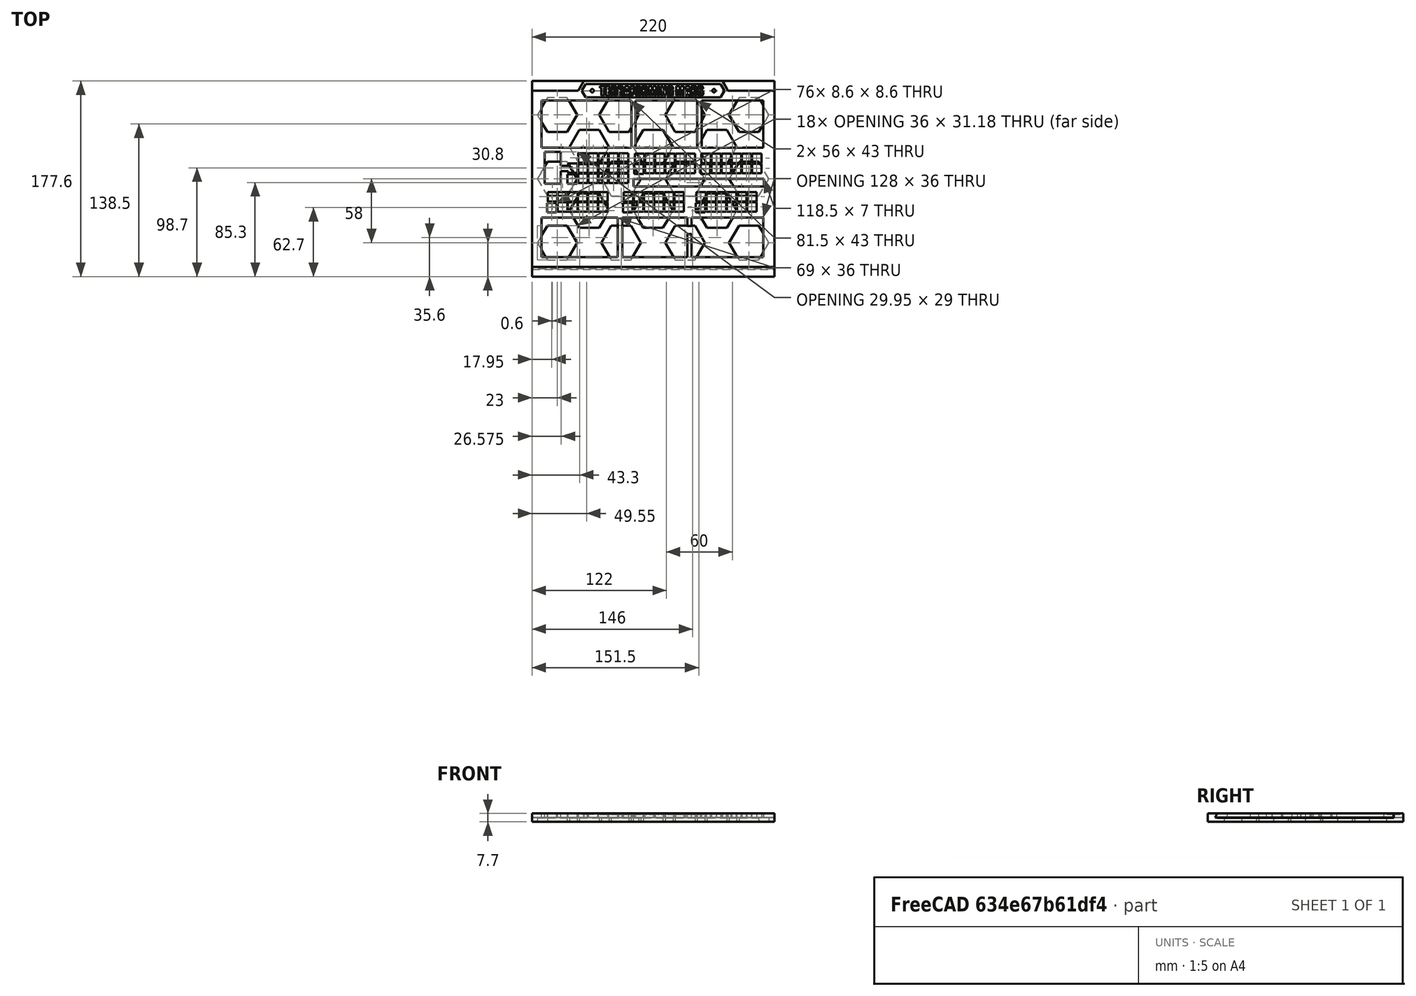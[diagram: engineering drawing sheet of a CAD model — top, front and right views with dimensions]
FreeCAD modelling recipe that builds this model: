
FCSTD DOCUMENT  (FreeCAD 0.21R33668 +26 (Git))
Label: overlay-full-v4
License: All rights reserved
LicenseURL: https://en.wikipedia.org/wiki/All_rights_reserved
objects: Sketcher::SketchObject×11, PartDesign::Pad×9, PartDesign::Pocket×5, Part::Feature×2, Part::Part2DObjectPython×2, PartDesign::Body×2, Mesh::Feature×1, Part::Refine×1, PartDesign::FeatureBase×1, Part::Extrusion×1
note: 48 computed .brp shape members not serialized (recipe doc carries the construction recipe); baked Part::Feature solids carry a one-line shape summary decoded from their .brp

FEATURE [Mesh::Feature] Terraforming_Mars_overlay
FEATURE [Part::Feature] Terraforming_Mars_overlay001
  shape: bbox 208 x 148 x 3.7 mm, 1736 faces, 0 solids (baked)
FEATURE [Part::Feature] Terraforming_Mars_overlay001_solid  label="Terraforming_Mars_overlay001 (Solid)"
  shape: bbox 208 x 148 x 3.7 mm, 1736 faces (baked)
FEATURE [Part::Refine] Terraforming_Mars_overlay001_solid001  label="Terraforming_Mars_overlay001 (Solid)001"
  Source = -> Terraforming_Mars_overlay001_solid
FEATURE [PartDesign::FeatureBase] BaseFeature
  BaseFeature = -> Terraforming_Mars_overlay001_solid001
FEATURE [Sketcher::SketchObject] Sketch
  ExternalGeometry = -> [BaseFeature]
  FullyConstrained = true
  MapMode = 5
  Placement = pos=(0,0,3.7) rot=(0,0,1;0rad)
  Support = -> [BaseFeature]
  sketch-geometry (8):
    g0: LineSegment StartX=6 StartY=154 StartZ=0 EndX=214 EndY=154 EndZ=0
    g1: LineSegment StartX=214 StartY=154 StartZ=0 EndX=214 EndY=6 EndZ=0
    g2: LineSegment StartX=214 StartY=6 StartZ=0 EndX=6 EndY=6 EndZ=0
    g3: LineSegment StartX=6 StartY=6 StartZ=0 EndX=6 EndY=154 EndZ=0
    g4: LineSegment StartX=0 StartY=160 StartZ=0 EndX=220 EndY=160 EndZ=0
    g5: LineSegment StartX=220 StartY=160 StartZ=0 EndX=220 EndY=0 EndZ=0
    g6: LineSegment StartX=220 StartY=0 StartZ=0 EndX=0 EndY=0 EndZ=0
    g7: LineSegment StartX=0 StartY=0 StartZ=0 EndX=0 EndY=160 EndZ=0
  constraints (22):
    c: Coincident(g0,g1)
    c: Coincident(g1,g2)
    c: Coincident(g2,g3)
    c: Coincident(g3,g0)
    c: Horizontal(g0)
    c: Horizontal(g2)
    c: Vertical(g1)
    c: Vertical(g3)
    c: Coincident(g0,g-3)
    c: Coincident(g1,g-4)
    c: Coincident(g4,g5)
    c: Coincident(g5,g6)
    c: Coincident(g6,g7)
    c: Coincident(g7,g4)
    c: Horizontal(g4)
    c: Horizontal(g6)
    c: Vertical(g5)
    c: Vertical(g7)
    c: DistanceX(g4,g0) = 6
    c: DistanceX(g0,g4) = 6
    c: DistanceY(g0,g4) = 6
    c: DistanceY(g5,g1) = 6
FEATURE [PartDesign::Pad] Pad
  BaseFeature = -> BaseFeature
  Direction = (0,0,1)
  Length = 10
  Length2 = 10
  Profile = -> Sketch
  ReferenceAxis = -> Sketch [N_Axis]
  Type = 3
  UpToFace = -> BaseFeature [Face1]
FEATURE [Sketcher::SketchObject] Sketch001
  ExternalGeometry = -> [Pad]
  FullyConstrained = true
  MapMode = 5
  Placement = pos=(0,0,3.7) rot=(0,0,1;0rad)
  Support = -> [Pad]
  sketch-geometry (5):
    g0: GeomPoint X=110 Y=160 Z=0
    g1: LineSegment StartX=42 StartY=160 StartZ=0 EndX=47.0807 EndY=168.8 EndZ=0
    g2: LineSegment StartX=47.0807 StartY=168.8 StartZ=0 EndX=172.919 EndY=168.8 EndZ=0
    g3: LineSegment StartX=172.919 StartY=168.8 StartZ=0 EndX=178 EndY=160 EndZ=0
    g4: LineSegment StartX=178 StartY=160 StartZ=0 EndX=42 EndY=160 EndZ=0
  constraints (13):
    c: Symmetric(g-3,g-3,g0)
    c: Coincident(g1,g2)
    c: Horizontal(g2)
    c: Coincident(g2,g3)
    c: Coincident(g3,g4)
    c: Coincident(g4,g1)
    c: Angle(g1,g4,g1) = 2.0944
    c: Angle(g4,g3,g3) = 2.0944
    c: DistanceY(g1,g1) = 8.8
    c: PointOnObject(g1,g-3)
    c: DistanceX(g-3,g1) = 42
    c: DistanceX(g3,g-3) = 42
    c: PointOnObject(g3,g-3)
FEATURE [PartDesign::Pad] Pad001
  BaseFeature = -> Pad
  Direction = (0,0,1)
  Length = 10
  Length2 = 10
  Profile = -> Sketch001
  ReferenceAxis = -> Sketch001 [N_Axis]
  Type = 3
  UpToFace = -> Pad [Face2]
FEATURE [Sketcher::SketchObject] Sketch002
  ExternalGeometry = -> [Pad001]
  FullyConstrained = true
  MapMode = 5
  Placement = pos=(0,0,3.7) rot=(0,0,1;0rad)
  Support = -> [Pad001]
  sketch-geometry (7):
    g0: GeomPoint X=110 Y=160 Z=0
    g1: LineSegment StartX=45.2332 StartY=160 StartZ=0 EndX=48.6973 EndY=166 EndZ=0
    g2: LineSegment StartX=48.6973 StartY=166 StartZ=0 EndX=171.303 EndY=166 EndZ=0
    g3: LineSegment StartX=171.303 StartY=166 StartZ=0 EndX=174.767 EndY=160 EndZ=0
    g4: LineSegment StartX=174.767 StartY=160 StartZ=0 EndX=171.303 EndY=154 EndZ=0
    g5: LineSegment StartX=171.303 StartY=154 StartZ=0 EndX=48.6973 EndY=154 EndZ=0
    g6: LineSegment StartX=48.6973 StartY=154 StartZ=0 EndX=45.2332 EndY=160 EndZ=0
  constraints (17):
    c: Symmetric(g-4,g-4,g0)
    c: PointOnObject(g1,g-4)
    c: Coincident(g1,g2)
    c: Horizontal(g2)
    c: Coincident(g2,g3)
    c: PointOnObject(g3,g-4)
    c: Coincident(g3,g4)
    c: PointOnObject(g4,g-5)
    c: Coincident(g4,g5)
    c: Coincident(g5,g6)
    c: Coincident(g6,g1)
    c: Parallel(g1,g-6)
    c: Symmetric(g5,g1,g-4)
    c: Symmetric(g4,g2,g-4)
    c: Parallel(g3,g-7)
    c: Distance(g1,g-6) = 2.8
    c: Distance(g2,g-7) = 2.8
FEATURE [PartDesign::Pocket] Pocket
  BaseFeature = -> Pad001
  Direction = (0,0,-1)
  Length = 1
  Length2 = 5
  Profile = -> Sketch002
  ReferenceAxis = -> Sketch002 [N_Axis]
  Type = 0
FEATURE [Part::Part2DObjectPython] ShapeString  # Draft 2D object (typed FeaturePython)
  FontFile = <path>
  MakeFace = true
  Placement = pos=(61.7,155.5,2.7) rot=(0,0,1;0rad)
  Size = 9
  String = TERRAFORMING MARS
  Tracking = 0
FEATURE [Sketcher::SketchObject] Sketch003
  ExternalGeometry = -> [Pocket]
  FullyConstrained = true
  MapMode = 5
  Placement = pos=(0,0,2.7) rot=(0,0,1;0rad)
  Support = -> [Pocket]
  sketch-geometry (3):
    g0: LineSegment StartX=45.2332 StartY=160 StartZ=0 EndX=174.767 EndY=160 EndZ=0
    g1: Circle CenterX=54.7332 CenterY=160 CenterZ=0 NormalX=0 NormalY=0 NormalZ=1 AngleXU=0 Radius=1.5
    g2: Circle CenterX=165.267 CenterY=160 CenterZ=0 NormalX=0 NormalY=0 NormalZ=1 AngleXU=0 Radius=1.5
  constraints (8):
    c: Coincident(g0,g-3)
    c: Coincident(g0,g-4)
    c: PointOnObject(g1,g0)
    c: PointOnObject(g2,g0)
    c: Diameter(g2) = 3
    c: Diameter(g1) = 3
    c: DistanceX(g0,g1) = 9.5
    c: DistanceX(g2,g0) = 9.5
FEATURE [PartDesign::Pad] Pad002
  BaseFeature = -> Pocket
  Direction = (0,0,1)
  Length = 1
  Length2 = 10
  Profile = -> Sketch003
  ReferenceAxis = -> Sketch003 [N_Axis]
  Type = 0
FEATURE [PartDesign::Pad] Pad003
  BaseFeature = -> Pad002
  Direction = (0,-1,0)
  Length = 2
  Length2 = 10
  Profile = -> Pad002 [Face352]
  Type = 0
FEATURE [Sketcher::SketchObject] Sketch004
  ExternalGeometry = -> [Pad003]
  FullyConstrained = true
  MapMode = 5
  Placement = pos=(220,0,0) rot=(0.57735,0.57735,0.57735;2.0944rad)
  Support = -> [Pad003]
  sketch-geometry (3):
    g0: LineSegment StartX=0 StartY=3.7 StartZ=0 EndX=-2 EndY=0 EndZ=0
    g1: LineSegment StartX=-2 StartY=0 StartZ=0 EndX=-2 EndY=3.7 EndZ=0
    g2: LineSegment StartX=-2 StartY=3.7 StartZ=0 EndX=0 EndY=3.7 EndZ=0
  constraints (6):
    c: Coincident(g-4,g0)
    c: Coincident(g0,g-3)
    c: Coincident(g0,g1)
    c: Coincident(g1,g-4)
    c: Coincident(g1,g2)
    c: Coincident(g2,g0)
FEATURE [PartDesign::Pocket] Pocket001
  BaseFeature = -> Pad003
  Direction = (-1,0,0)
  Length = 5
  Length2 = 5
  Profile = -> Sketch004
  ReferenceAxis = -> Sketch004 [N_Axis]
  Type = 1
FEATURE [PartDesign::Body] Body  label="Front"
  BaseFeature = -> Terraforming_Mars_overlay001_solid001
  Group = -> [BaseFeature,Sketch,Pad,Sketch001,Pad001,Sketch002,Pocket,Sketch003,Pad002,Pad003,Sketch004,Pocket001]
  Origin = -> Origin
  Tip = -> Pocket001
FEATURE [Part::Extrusion] Extrude  label="Text"
  Base = -> ShapeString
  Dir = (0,0,1)
  DirMode = 2
  FaceMakerClass = Part::FaceMakerBullseye
  LengthFwd = 1
  LengthRev = 0
  Solid = false
  Symmetric = false
FEATURE [Sketcher::SketchObject] Sketch005
  FullyConstrained = true
  MapMode = 5
  Support = -> [XY_Plane001]
  sketch-geometry (4):
    g0: LineSegment StartX=0 StartY=160 StartZ=0 EndX=220 EndY=160 EndZ=0
    g1: LineSegment StartX=220 StartY=160 StartZ=0 EndX=220 EndY=0 EndZ=0
    g2: LineSegment StartX=220 StartY=0 StartZ=0 EndX=0 EndY=0 EndZ=0
    g3: LineSegment StartX=0 StartY=0 StartZ=0 EndX=0 EndY=160 EndZ=0
  constraints (12):
    c: Coincident(g0,g1)
    c: Coincident(g1,g2)
    c: Coincident(g2,g3)
    c: Coincident(g3,g0)
    c: Horizontal(g0)
    c: Horizontal(g2)
    c: Vertical(g1)
    c: Vertical(g3)
    c: PointOnObject(g1,g-1)
    c: PointOnObject(g0,g-2)
    c: DistanceX(g0,g0) = 220
    c: DistanceY(g1,g1) = 160
FEATURE [PartDesign::Pad] Pad004
  Direction = (0,0,1)
  Length = 4
  Length2 = 10
  Profile = -> Sketch005
  ReferenceAxis = -> Sketch005 [N_Axis]
  Reversed = true
  Type = 0
FEATURE [PartDesign::Pad] Pad005
  BaseFeature = -> Pad004
  Direction = (0,-1,0)
  Length = 8.8
  Length2 = 10
  Profile = -> Pad004 [Face3]
  Type = 0
FEATURE [PartDesign::Pad] Pad006
  BaseFeature = -> Pad005
  Direction = (0,0,1)
  Length = 3.7
  Length2 = 10
  Profile = -> Pad005 [Face8]
  Type = 0
FEATURE [Sketcher::SketchObject] Sketch006
  ExternalGeometry = -> [Pad006]
  FullyConstrained = true
  MapMode = 5
  Placement = pos=(0,0,0) rot=(0.57735,-0.57735,-0.57735;2.0944rad)
  Support = -> [Pad006]
  sketch-geometry (4):
    g0: LineSegment StartX=0 StartY=0 StartZ=0 EndX=2.1 EndY=0 EndZ=0
    g1: LineSegment StartX=0.1 StartY=3.7 StartZ=0 EndX=2.1 EndY=0 EndZ=0
    g2: LineSegment StartX=0 StartY=3.7 StartZ=0 EndX=0 EndY=0 EndZ=0
    g3: LineSegment StartX=0.1 StartY=3.7 StartZ=0 EndX=0 EndY=3.7 EndZ=0
  constraints (10):
    c: Coincident(g-1,g0)
    c: PointOnObject(g0,g-1)
    c: Coincident(g1,g0)
    c: DistanceX(g0,g0) = 2.1
    c: PointOnObject(g1,g-3)
    c: Coincident(g2,g-3)
    c: Coincident(g2,g0)
    c: Coincident(g3,g1)
    c: Coincident(g3,g2)
    c: DistanceX(g3,g3) = 0.1
FEATURE [PartDesign::Pocket] Pocket002
  BaseFeature = -> Pad006
  Direction = (1,0,0)
  Length = 5
  Length2 = 5
  Profile = -> Sketch006
  ReferenceAxis = -> Sketch006 [N_Axis]
  Type = 1
FEATURE [PartDesign::Pad] Pad007
  BaseFeature = -> Pocket002
  Direction = (0,1,0)
  Length = 8.8
  Length2 = 10
  Profile = -> Pocket002 [Face1]
  Type = 0
FEATURE [Sketcher::SketchObject] Sketch007
  ExternalGeometry = -> [Pad007]
  FullyConstrained = true
  MapMode = 5
  Placement = pos=(0,0,0) rot=(0.57735,-0.57735,-0.57735;2.0944rad)
  Support = -> [Pad007]
  sketch-geometry (3):
    g0: LineSegment StartX=4.63784 StartY=3.7 StartZ=0 EndX=8.8 EndY=-4 EndZ=0
    g1: LineSegment StartX=8.8 StartY=-4 StartZ=0 EndX=8.8 EndY=3.7 EndZ=0
    g2: LineSegment StartX=8.8 StartY=3.7 StartZ=0 EndX=4.63784 EndY=3.7 EndZ=0
  constraints (7):
    c: PointOnObject(g0,g-3)
    c: Coincident(g0,g-6)
    c: Coincident(g1,g0)
    c: Coincident(g1,g-5)
    c: Coincident(g2,g1)
    c: Coincident(g2,g0)
    c: Parallel(g0,g-4)
FEATURE [Sketcher::SketchObject] Sketch008
  ExternalGeometry = -> [Pad007]
  FullyConstrained = true
  MapMode = 5
  Support = -> [Pad007]
  sketch-geometry (12):
    g0: LineSegment StartX=0 StartY=160 StartZ=0 EndX=42 EndY=160 EndZ=0
    g1: LineSegment StartX=42 StartY=160 StartZ=0 EndX=47.0807 EndY=168.8 EndZ=0
    g2: LineSegment StartX=0 StartY=168.8 StartZ=0 EndX=46.9652 EndY=168.8 EndZ=0
    g3: LineSegment StartX=46.9652 StartY=168.8 StartZ=0 EndX=41.9423 EndY=160.1 EndZ=0
    g4: LineSegment StartX=41.9423 StartY=160.1 StartZ=0 EndX=0 EndY=160.1 EndZ=0
    g5: LineSegment StartX=0 StartY=160.1 StartZ=0 EndX=0 EndY=168.8 EndZ=0
    g6: LineSegment StartX=172.919 StartY=168.8 StartZ=0 EndX=178 EndY=160 EndZ=0
    g7: LineSegment StartX=178 StartY=160 StartZ=0 EndX=220 EndY=160 EndZ=0
    g8: LineSegment StartX=173.035 StartY=168.8 StartZ=0 EndX=220 EndY=168.8 EndZ=0
    g9: LineSegment StartX=220 StartY=168.8 StartZ=0 EndX=220 EndY=160.1 EndZ=0
    g10: LineSegment StartX=220 StartY=160.1 StartZ=0 EndX=178.058 EndY=160.1 EndZ=0
    g11: LineSegment StartX=178.058 StartY=160.1 StartZ=0 EndX=173.035 EndY=168.8 EndZ=0
  constraints (34):
    c: Coincident(g-4,g0)
    c: PointOnObject(g0,g-4)
    c: Coincident(g0,g1)
    c: PointOnObject(g1,g-3)
    c: DistanceX(g0,g0) = 42
    c: Angle(g-4,g1,g0) = 1.0472
    c: Coincident(g-3,g2)
    c: PointOnObject(g2,g-3)
    c: Coincident(g2,g3)
    c: Coincident(g3,g4)
    c: PointOnObject(g4,g-2)
    c: Horizontal(g4)
    c: Coincident(g4,g5)
    c: Coincident(g5,g2)
    c: Parallel(g3,g1)
    c: Distance(g4,g0) = 0.1
    c: Distance(g2,g1) = 0.1
    c: PointOnObject(g6,g-3)
    c: PointOnObject(g6,g-4)
    c: Coincident(g7,g6)
    c: Coincident(g7,g-5)
    c: DistanceX(g7,g7) = 42
    c: Angle(g6,g-4,g6) = 1.0472
    c: PointOnObject(g8,g-3)
    c: Coincident(g8,g-5)
    c: Coincident(g8,g9)
    c: PointOnObject(g9,g-5)
    c: Coincident(g9,g10)
    c: Horizontal(g10)
    c: Coincident(g10,g11)
    c: Coincident(g11,g8)
    c: Distance(g8,g6) = 0.1
    c: Parallel(g11,g6)
    c: Distance(g9,g7) = 0.1
FEATURE [PartDesign::Pad] Pad008
  BaseFeature = -> Pad007
  Direction = (0,0,1)
  Length = 3.7
  Length2 = 10
  Profile = -> Sketch008
  ReferenceAxis = -> Sketch008 [N_Axis]
  Type = 0
FEATURE [Sketcher::SketchObject] Sketch009
  ExternalGeometry = -> [Pad008]
  FullyConstrained = true
  MapMode = 5
  Support = -> [Pad008]
  sketch-geometry (4):
    g0: LineSegment StartX=0 StartY=0 StartZ=0 EndX=220 EndY=0 EndZ=0
    g1: LineSegment StartX=220 StartY=0 StartZ=0 EndX=220 EndY=160 EndZ=0
    g2: LineSegment StartX=220 StartY=160 StartZ=0 EndX=0 EndY=160 EndZ=0
    g3: LineSegment StartX=0 StartY=160 StartZ=0 EndX=0 EndY=0 EndZ=0
  constraints (10):
    c: Coincident(g0,g1)
    c: Coincident(g1,g2)
    c: Coincident(g2,g3)
    c: Coincident(g3,g0)
    c: Horizontal(g0)
    c: Horizontal(g2)
    c: Vertical(g1)
    c: Vertical(g3)
    c: Coincident(g0,g-5)
    c: Coincident(g1,g-4)
FEATURE [PartDesign::Pocket] Pocket003
  BaseFeature = -> Pad008
  Direction = (0,0,-1)
  Length = 0.3
  Length2 = 5
  Profile = -> Sketch009
  ReferenceAxis = -> Sketch009 [N_Axis]
  Type = 0
FEATURE [Part::Part2DObjectPython] ShapeString001  # Draft 2D object (typed FeaturePython)
  FontFile = <path>
  MakeFace = true
  Placement = pos=(12.35,20,0) rot=(0,0,1;1e-06rad)
  Size = 120
  String = T M
  Tracking = 0
FEATURE [Sketcher::SketchObject] Sketch010
  ExternalGeometry = -> [Pocket003]
  FullyConstrained = true
  MapMode = 5
  Placement = pos=(0,0,-0.3) rot=(0,0,1;0rad)
  Support = -> [Pocket003]
  sketch-geometry (138):
    g0: LineSegment StartX=220 StartY=138 StartZ=0 EndX=0 EndY=138 EndZ=0
    g1: LineSegment StartX=220 StartY=109 StartZ=0 EndX=0 EndY=109 EndZ=0
    g2: LineSegment StartX=220 StartY=80 StartZ=0 EndX=0 EndY=80 EndZ=0
    g3: LineSegment StartX=0 StartY=51 StartZ=0 EndX=220 EndY=51 EndZ=0
    g4: LineSegment StartX=70 StartY=109 StartZ=0 EndX=61 EndY=124.588 EndZ=0
    g5: LineSegment StartX=61 StartY=124.588 StartZ=0 EndX=43 EndY=124.588 EndZ=0
    g6: LineSegment StartX=43 StartY=124.588 StartZ=0 EndX=34 EndY=109 EndZ=0
    g7: LineSegment StartX=34 StartY=109 StartZ=0 EndX=43 EndY=93.4115 EndZ=0
    g8: LineSegment StartX=43 StartY=93.4115 StartZ=0 EndX=61 EndY=93.4115 EndZ=0
    g9: LineSegment StartX=61 StartY=93.4115 StartZ=0 EndX=70 EndY=109 EndZ=0
    g10: Circle CenterX=52 CenterY=109 CenterZ=0 NormalX=0 NormalY=0 NormalZ=1 AngleXU=0 Radius=18
    g11: LineSegment StartX=41 StartY=138 StartZ=0 EndX=32 EndY=153.588 EndZ=0
    g12: LineSegment StartX=32 StartY=153.588 StartZ=0 EndX=14 EndY=153.588 EndZ=0
    g13: LineSegment StartX=14 StartY=153.588 StartZ=0 EndX=5 EndY=138 EndZ=0
    g14: LineSegment StartX=5 StartY=138 StartZ=0 EndX=14 EndY=122.412 EndZ=0
    g15: LineSegment StartX=14 StartY=122.412 StartZ=0 EndX=32 EndY=122.412 EndZ=0
    g16: LineSegment StartX=32 StartY=122.412 StartZ=0 EndX=41 EndY=138 EndZ=0
    g17: Circle CenterX=23 CenterY=138 CenterZ=0 NormalX=0 NormalY=0 NormalZ=1 AngleXU=0 Radius=18
    g18: LineSegment StartX=97 StartY=138 StartZ=0 EndX=88 EndY=153.588 EndZ=0
    g19: LineSegment StartX=88 StartY=153.588 StartZ=0 EndX=70 EndY=153.588 EndZ=0
    g20: LineSegment StartX=70 StartY=153.588 StartZ=0 EndX=61 EndY=138 EndZ=0
    g21: LineSegment StartX=61 StartY=138 StartZ=0 EndX=70 EndY=122.412 EndZ=0
    g22: LineSegment StartX=70 StartY=122.412 StartZ=0 EndX=88 EndY=122.412 EndZ=0
    g23: LineSegment StartX=88 StartY=122.412 StartZ=0 EndX=97 EndY=138 EndZ=0
    g24: Circle CenterX=79 CenterY=138 CenterZ=0 NormalX=0 NormalY=0 NormalZ=1 AngleXU=0 Radius=18
    g25: LineSegment StartX=0 StartY=22 StartZ=0 EndX=220 EndY=22 EndZ=0
    g26: LineSegment StartX=128 StartY=109 StartZ=0 EndX=119 EndY=124.588 EndZ=0
    g27: LineSegment StartX=119 StartY=124.588 StartZ=0 EndX=101 EndY=124.588 EndZ=0
    g28: LineSegment StartX=101 StartY=124.588 StartZ=0 EndX=92 EndY=109 EndZ=0
    g29: LineSegment StartX=92 StartY=109 StartZ=0 EndX=101 EndY=93.4115 EndZ=0
    g30: LineSegment StartX=101 StartY=93.4115 StartZ=0 EndX=119 EndY=93.4115 EndZ=0
    g31: LineSegment StartX=119 StartY=93.4115 StartZ=0 EndX=128 EndY=109 EndZ=0
    g32: Circle CenterX=110 CenterY=109 CenterZ=0 NormalX=0 NormalY=0 NormalZ=1 AngleXU=0 Radius=18
    g33: LineSegment StartX=157 StartY=138 StartZ=0 EndX=148 EndY=153.588 EndZ=0
    g34: LineSegment StartX=148 StartY=153.588 StartZ=0 EndX=130 EndY=153.588 EndZ=0
    g35: LineSegment StartX=130 StartY=153.588 StartZ=0 EndX=121 EndY=138 EndZ=0
    g36: LineSegment StartX=121 StartY=138 StartZ=0 EndX=130 EndY=122.412 EndZ=0
    g37: LineSegment StartX=130 StartY=122.412 StartZ=0 EndX=148 EndY=122.412 EndZ=0
    g38: LineSegment StartX=148 StartY=122.412 StartZ=0 EndX=157 EndY=138 EndZ=0
    g39: Circle CenterX=139 CenterY=138 CenterZ=0 NormalX=0 NormalY=0 NormalZ=1 AngleXU=0 Radius=18
    g40: LineSegment StartX=23 StartY=160 StartZ=0 EndX=23 EndY=0 EndZ=0
    g41: LineSegment StartX=52 StartY=160 StartZ=0 EndX=52 EndY=0 EndZ=0
    g42: LineSegment StartX=81 StartY=160 StartZ=0 EndX=81 EndY=0 EndZ=0
    g43: LineSegment StartX=110 StartY=160 StartZ=0 EndX=110 EndY=0 EndZ=0
    g44: LineSegment StartX=139 StartY=160 StartZ=0 EndX=139 EndY=0 EndZ=0
    g45: LineSegment StartX=168 StartY=160 StartZ=0 EndX=168 EndY=0 EndZ=0
    g46: LineSegment StartX=197 StartY=160 StartZ=0 EndX=197 EndY=0 EndZ=0
    g47: LineSegment StartX=186 StartY=109 StartZ=0 EndX=177 EndY=124.588 EndZ=0
    g48: LineSegment StartX=177 StartY=124.588 StartZ=0 EndX=159 EndY=124.588 EndZ=0
    g49: LineSegment StartX=159 StartY=124.588 StartZ=0 EndX=150 EndY=109 EndZ=0
    g50: LineSegment StartX=150 StartY=109 StartZ=0 EndX=159 EndY=93.4115 EndZ=0
    g51: LineSegment StartX=159 StartY=93.4115 StartZ=0 EndX=177 EndY=93.4115 EndZ=0
    g52: LineSegment StartX=177 StartY=93.4115 StartZ=0 EndX=186 EndY=109 EndZ=0
    g53: Circle CenterX=168 CenterY=109 CenterZ=0 NormalX=0 NormalY=0 NormalZ=1 AngleXU=0 Radius=18
    g54: LineSegment StartX=215 StartY=138 StartZ=0 EndX=206 EndY=153.588 EndZ=0
    g55: LineSegment StartX=206 StartY=153.588 StartZ=0 EndX=188 EndY=153.588 EndZ=0
    g56: LineSegment StartX=188 StartY=153.588 StartZ=0 EndX=179 EndY=138 EndZ=0
    g57: LineSegment StartX=179 StartY=138 StartZ=0 EndX=188 EndY=122.412 EndZ=0
    g58: LineSegment StartX=188 StartY=122.412 StartZ=0 EndX=206 EndY=122.412 EndZ=0
    g59: LineSegment StartX=206 StartY=122.412 StartZ=0 EndX=215 EndY=138 EndZ=0
    g60: Circle CenterX=197 CenterY=138 CenterZ=0 NormalX=0 NormalY=0 NormalZ=1 AngleXU=0 Radius=18
    g61: LineSegment StartX=215 StartY=80 StartZ=0 EndX=206 EndY=95.5885 EndZ=0
    g62: LineSegment StartX=206 StartY=95.5885 StartZ=0 EndX=188 EndY=95.5885 EndZ=0
    g63: LineSegment StartX=188 StartY=95.5885 StartZ=0 EndX=179 EndY=80 EndZ=0
    g64: LineSegment StartX=179 StartY=80 StartZ=0 EndX=188 EndY=64.4115 EndZ=0
    g65: LineSegment StartX=188 StartY=64.4115 StartZ=0 EndX=206 EndY=64.4115 EndZ=0
    g66: LineSegment StartX=206 StartY=64.4115 StartZ=0 EndX=215 EndY=80 EndZ=0
    g67: Circle CenterX=197 CenterY=80 CenterZ=0 NormalX=0 NormalY=0 NormalZ=1 AngleXU=0 Radius=18
    g68: LineSegment StartX=186 StartY=51 StartZ=0 EndX=177 EndY=66.5885 EndZ=0
    g69: LineSegment StartX=177 StartY=66.5885 StartZ=0 EndX=159 EndY=66.5885 EndZ=0
    g70: LineSegment StartX=159 StartY=66.5885 StartZ=0 EndX=150 EndY=51 EndZ=0
    g71: LineSegment StartX=150 StartY=51 StartZ=0 EndX=159 EndY=35.4115 EndZ=0
    g72: LineSegment StartX=159 StartY=35.4115 StartZ=0 EndX=177 EndY=35.4115 EndZ=0
    g73: LineSegment StartX=177 StartY=35.4115 StartZ=0 EndX=186 EndY=51 EndZ=0
    g74: Circle CenterX=168 CenterY=51 CenterZ=0 NormalX=0 NormalY=0 NormalZ=1 AngleXU=0 Radius=18
    g75: LineSegment StartX=157 StartY=80 StartZ=0 EndX=148 EndY=95.5885 EndZ=0
    g76: LineSegment StartX=148 StartY=95.5885 StartZ=0 EndX=130 EndY=95.5885 EndZ=0
    g77: LineSegment StartX=130 StartY=95.5885 StartZ=0 EndX=121 EndY=80 EndZ=0
    g78: LineSegment StartX=121 StartY=80 StartZ=0 EndX=130 EndY=64.4115 EndZ=0
    g79: LineSegment StartX=130 StartY=64.4115 StartZ=0 EndX=148 EndY=64.4115 EndZ=0
    g80: LineSegment StartX=148 StartY=64.4115 StartZ=0 EndX=157 EndY=80 EndZ=0
    g81: Circle CenterX=139 CenterY=80 CenterZ=0 NormalX=0 NormalY=0 NormalZ=1 AngleXU=0 Radius=18
    g82: LineSegment StartX=99 StartY=80 StartZ=0 EndX=90 EndY=95.5885 EndZ=0
    g83: LineSegment StartX=90 StartY=95.5885 StartZ=0 EndX=72 EndY=95.5885 EndZ=0
    g84: LineSegment StartX=72 StartY=95.5885 StartZ=0 EndX=63 EndY=80 EndZ=0
    g85: LineSegment StartX=63 StartY=80 StartZ=0 EndX=72 EndY=64.4115 EndZ=0
    g86: LineSegment StartX=72 StartY=64.4115 StartZ=0 EndX=90 EndY=64.4115 EndZ=0
    g87: LineSegment StartX=90 StartY=64.4115 StartZ=0 EndX=99 EndY=80 EndZ=0
    g88: Circle CenterX=81 CenterY=80 CenterZ=0 NormalX=0 NormalY=0 NormalZ=1 AngleXU=0 Radius=18
    g89: LineSegment StartX=41 StartY=80 StartZ=0 EndX=32 EndY=95.5885 EndZ=0
    g90: LineSegment StartX=32 StartY=95.5885 StartZ=0 EndX=14 EndY=95.5885 EndZ=0
    g91: LineSegment StartX=14 StartY=95.5885 StartZ=0 EndX=5 EndY=80 EndZ=0
    g92: LineSegment StartX=5 StartY=80 StartZ=0 EndX=14 EndY=64.4115 EndZ=0
    g93: LineSegment StartX=14 StartY=64.4115 StartZ=0 EndX=32 EndY=64.4115 EndZ=0
    g94: LineSegment StartX=32 StartY=64.4115 StartZ=0 EndX=41 EndY=80 EndZ=0
    g95: Circle CenterX=23 CenterY=80 CenterZ=0 NormalX=0 NormalY=0 NormalZ=1 AngleXU=0 Radius=18
    g96: LineSegment StartX=70 StartY=51 StartZ=0 EndX=61 EndY=66.5885 EndZ=0
    g97: LineSegment StartX=61 StartY=66.5885 StartZ=0 EndX=43 EndY=66.5885 EndZ=0
    g98: LineSegment StartX=43 StartY=66.5885 StartZ=0 EndX=34 EndY=51 EndZ=0
    g99: LineSegment StartX=34 StartY=51 StartZ=0 EndX=43 EndY=35.4115 EndZ=0
    g100: LineSegment StartX=43 StartY=35.4115 StartZ=0 EndX=61 EndY=35.4115 EndZ=0
    g101: LineSegment StartX=61 StartY=35.4115 StartZ=0 EndX=70 EndY=51 EndZ=0
    g102: Circle CenterX=52 CenterY=51 CenterZ=0 NormalX=0 NormalY=0 NormalZ=1 AngleXU=0 Radius=18
    g103: LineSegment StartX=128 StartY=51 StartZ=0 EndX=119 EndY=66.5885 EndZ=0
    g104: LineSegment StartX=119 StartY=66.5885 StartZ=0 EndX=101 EndY=66.5885 EndZ=0
    g105: LineSegment StartX=101 StartY=66.5885 StartZ=0 EndX=92 EndY=51 EndZ=0
    g106: LineSegment StartX=92 StartY=51 StartZ=0 EndX=101 EndY=35.4115 EndZ=0
    g107: LineSegment StartX=101 StartY=35.4115 StartZ=0 EndX=119 EndY=35.4115 EndZ=0
    g108: LineSegment StartX=119 StartY=35.4115 StartZ=0 EndX=128 EndY=51 EndZ=0
    g109: Circle CenterX=110 CenterY=51 CenterZ=0 NormalX=0 NormalY=0 NormalZ=1 AngleXU=0 Radius=18
    g110: LineSegment StartX=41 StartY=22 StartZ=0 EndX=32 EndY=37.5885 EndZ=0
    g111: LineSegment StartX=32 StartY=37.5885 StartZ=0 EndX=14 EndY=37.5885 EndZ=0
    g112: LineSegment StartX=14 StartY=37.5885 StartZ=0 EndX=5 EndY=22 EndZ=0
    g113: LineSegment StartX=5 StartY=22 StartZ=0 EndX=14 EndY=6.41154 EndZ=0
    g114: LineSegment StartX=14 StartY=6.41154 StartZ=0 EndX=32 EndY=6.41154 EndZ=0
    g115: LineSegment StartX=32 StartY=6.41154 StartZ=0 EndX=41 EndY=22 EndZ=0
    g116: Circle CenterX=23 CenterY=22 CenterZ=0 NormalX=0 NormalY=0 NormalZ=1 AngleXU=0 Radius=18
    g117: LineSegment StartX=99 StartY=22 StartZ=0 EndX=90 EndY=37.5885 EndZ=0
    g118: LineSegment StartX=90 StartY=37.5885 StartZ=0 EndX=72 EndY=37.5885 EndZ=0
    g119: LineSegment StartX=72 StartY=37.5885 StartZ=0 EndX=63 EndY=22 EndZ=0
    g120: LineSegment StartX=63 StartY=22 StartZ=0 EndX=72 EndY=6.41154 EndZ=0
    g121: LineSegment StartX=72 StartY=6.41154 StartZ=0 EndX=90 EndY=6.41154 EndZ=0
    g122: LineSegment StartX=90 StartY=6.41154 StartZ=0 EndX=99 EndY=22 EndZ=0
    g123: Circle CenterX=81 CenterY=22 CenterZ=0 NormalX=0 NormalY=0 NormalZ=1 AngleXU=0 Radius=18
    g124: LineSegment StartX=157 StartY=22 StartZ=0 EndX=148 EndY=37.5885 EndZ=0
    g125: LineSegment StartX=148 StartY=37.5885 StartZ=0 EndX=130 EndY=37.5885 EndZ=0
    g126: LineSegment StartX=130 StartY=37.5885 StartZ=0 EndX=121 EndY=22 EndZ=0
    g127: LineSegment StartX=121 StartY=22 StartZ=0 EndX=130 EndY=6.41154 EndZ=0
    g128: LineSegment StartX=130 StartY=6.41154 StartZ=0 EndX=148 EndY=6.41154 EndZ=0
    g129: LineSegment StartX=148 StartY=6.41154 StartZ=0 EndX=157 EndY=22 EndZ=0
    g130: Circle CenterX=139 CenterY=22 CenterZ=0 NormalX=0 NormalY=0 NormalZ=1 AngleXU=0 Radius=18
    g131: LineSegment StartX=215 StartY=22 StartZ=0 EndX=206 EndY=37.5885 EndZ=0
    g132: LineSegment StartX=206 StartY=37.5885 StartZ=0 EndX=188 EndY=37.5885 EndZ=0
    g133: LineSegment StartX=188 StartY=37.5885 StartZ=0 EndX=179 EndY=22 EndZ=0
    g134: LineSegment StartX=179 StartY=22 StartZ=0 EndX=188 EndY=6.41154 EndZ=0
    g135: LineSegment StartX=188 StartY=6.41154 StartZ=0 EndX=206 EndY=6.41154 EndZ=0
    g136: LineSegment StartX=206 StartY=6.41154 StartZ=0 EndX=215 EndY=22 EndZ=0
    g137: Circle CenterX=197 CenterY=22 CenterZ=0 NormalX=0 NormalY=0 NormalZ=1 AngleXU=0 Radius=18
  constraints (354):
    c: PointOnObject(g0,g-5)
    c: Horizontal(g0)
    c: PointOnObject(g1,g-5)
    c: PointOnObject(g1,g-3)
    c: Horizontal(g1)
    c: PointOnObject(g2,g-5)
    c: PointOnObject(g2,g-2)
    c: Horizontal(g2)
    c: PointOnObject(g0,g-3)
    c: DistanceY(g0,g-4) = 22
    c: DistanceY(g1,g0) = 29
    c: DistanceY(g2,g1) = 29
    c: PointOnObject(g3,g-3)
    c: PointOnObject(g3,g-5)
    c: Horizontal(g3)
    c: DistanceY(g3,g2) = 29
    c: Coincident(g4,g5)
    c: Coincident(g5,g6)
    c: Coincident(g6,g7)
    c: Coincident(g7,g8)
    c: Coincident(g8,g9)
    c: Coincident(g9,g4)
    c: Equal(g4, g5-g9) x5
    c: PointOnObject(g4,g10)
    c: PointOnObject(g5,g10)
    c: PointOnObject(g6,g10)
    c: PointOnObject(g7,g10)
    c: PointOnObject(g8,g10)
    c: PointOnObject(g9,g10)
    c: PointOnObject(g10,g1)
    c: PointOnObject(g9,g1)
    c: Coincident(g11,g12)
    c: Coincident(g12,g13)
    c: Coincident(g13,g14)
    c: Coincident(g14,g15)
    c: Coincident(g15,g16)
    c: Coincident(g16,g11)
    c: Equal(g11, g12-g16) x5
    c: PointOnObject(g11,g17)
    c: PointOnObject(g12,g17)
    c: PointOnObject(g13,g17)
    c: PointOnObject(g14,g17)
    c: PointOnObject(g15,g17)
    c: PointOnObject(g16,g17)
    c: PointOnObject(g17,g0)
    c: PointOnObject(g16,g0)
    c: Coincident(g18,g19)
    c: Coincident(g19,g20)
    c: Coincident(g20,g21)
    c: Coincident(g21,g22)
    c: Coincident(g22,g23)
    c: Coincident(g23,g18)
    c: Equal(g18, g19-g23) x5
    c: PointOnObject(g18,g24)
    c: PointOnObject(g19,g24)
    c: PointOnObject(g20,g24)
    c: PointOnObject(g21,g24)
    c: PointOnObject(g22,g24)
    c: PointOnObject(g23,g24)
    c: PointOnObject(g24,g0)
    c: PointOnObject(g23,g0)
    c: PointOnObject(g25,g-3)
    c: PointOnObject(g25,g-5)
    c: Horizontal(g25)
    c: DistanceY(g25,g3) = 29
    c: Coincident(g26,g27)
    c: Coincident(g27,g28)
    c: Coincident(g28,g29)
    c: Coincident(g29,g30)
    c: Coincident(g30,g31)
    c: Coincident(g31,g26)
    c: Equal(g26, g27-g31) x5
    c: PointOnObject(g26,g32)
    c: PointOnObject(g27,g32)
    c: PointOnObject(g28,g32)
    c: PointOnObject(g29,g32)
    c: PointOnObject(g30,g32)
    c: PointOnObject(g31,g32)
    c: PointOnObject(g32,g1)
    c: PointOnObject(g31,g1)
    c: Coincident(g33,g34)
    c: Coincident(g34,g35)
    c: Coincident(g35,g36)
    c: Coincident(g36,g37)
    c: Coincident(g37,g38)
    c: Coincident(g38,g33)
    c: Equal(g33, g34-g38) x5
    c: PointOnObject(g33,g39)
    c: PointOnObject(g34,g39)
    c: PointOnObject(g35,g39)
    c: PointOnObject(g36,g39)
    c: PointOnObject(g37,g39)
    c: PointOnObject(g38,g39)
    c: PointOnObject(g39,g0)
    c: PointOnObject(g38,g0)
    c: DistanceX(g24,g39) = 60
    c: PointOnObject(g40,g-4)
    c: PointOnObject(g40,g-6)
    c: Vertical(g40)
    c: PointOnObject(g41,g-4)
    c: PointOnObject(g41,g-6)
    c: Vertical(g41)
    c: PointOnObject(g42,g-4)
    c: PointOnObject(g42,g-6)
    c: Vertical(g42)
    c: PointOnObject(g43,g-4)
    c: PointOnObject(g43,g-6)
    c: Vertical(g43)
    c: PointOnObject(g44,g-4)
    c: PointOnObject(g44,g-6)
    c: Vertical(g44)
    c: PointOnObject(g45,g-4)
    c: PointOnObject(g45,g-6)
    c: Vertical(g45)
    c: PointOnObject(g46,g-4)
    c: PointOnObject(g46,g-6)
    c: Vertical(g46)
    c: DistanceX(g40,g41) = 29
    c: DistanceX(g41,g42) = 29
    c: DistanceX(g42,g43) = 29
    c: DistanceX(g43,g44) = 29
    c: DistanceX(g44,g45) = 29
    c: DistanceX(g45,g46) = 29
    c: DistanceX(g-4,g40) = 23
    c: PointOnObject(g17,g40)
    c: Radius(g17) = 18
    c: PointOnObject(g10,g41)
    c: Radius(g10) = 18
    c: Radius(g24) = 18
    c: Radius(g32) = 18
    c: Radius(g39) = 18
    c: PointOnObject(g32,g43)
    c: PointOnObject(g39,g44)
    c: Coincident(g47,g48)
    c: Coincident(g48,g49)
    c: Coincident(g49,g50)
    c: Coincident(g50,g51)
    c: Coincident(g51,g52)
    c: Coincident(g52,g47)
    c: Equal(g47, g48-g52) x5
    c: PointOnObject(g47,g53)
    c: PointOnObject(g48,g53)
    c: PointOnObject(g49,g53)
    c: PointOnObject(g50,g53)
    c: PointOnObject(g51,g53)
    c: PointOnObject(g52,g53)
    c: PointOnObject(g53,g1)
    c: PointOnObject(g52,g1)
    c: Coincident(g54,g55)
    c: Coincident(g55,g56)
    c: Coincident(g56,g57)
    c: Coincident(g57,g58)
    c: Coincident(g58,g59)
    c: Coincident(g59,g54)
    c: Equal(g54, g55-g59) x5
    c: PointOnObject(g54,g60)
    c: PointOnObject(g55,g60)
    c: PointOnObject(g56,g60)
    c: PointOnObject(g57,g60)
    c: PointOnObject(g58,g60)
    c: PointOnObject(g59,g60)
    c: PointOnObject(g60,g0)
    c: PointOnObject(g59,g0)
    c: Coincident(g61,g62)
    c: Coincident(g62,g63)
    c: Coincident(g63,g64)
    c: Coincident(g64,g65)
    c: Coincident(g65,g66)
    c: Coincident(g66,g61)
    c: Equal(g61, g62-g66) x5
    c: PointOnObject(g61,g67)
    c: PointOnObject(g62,g67)
    c: PointOnObject(g63,g67)
    c: PointOnObject(g64,g67)
    c: PointOnObject(g65,g67)
    c: PointOnObject(g66,g67)
    c: PointOnObject(g67,g2)
    c: PointOnObject(g66,g2)
    c: Coincident(g68,g69)
    c: Coincident(g69,g70)
    c: Coincident(g70,g71)
    c: Coincident(g71,g72)
    c: Coincident(g72,g73)
    c: Coincident(g73,g68)
    c: Equal(g68, g69-g73) x5
    c: PointOnObject(g68,g74)
    c: PointOnObject(g69,g74)
    c: PointOnObject(g70,g74)
    c: PointOnObject(g71,g74)
    c: PointOnObject(g72,g74)
    c: PointOnObject(g73,g74)
    c: PointOnObject(g74,g3)
    c: PointOnObject(g73,g3)
    c: Coincident(g75,g76)
    c: Coincident(g76,g77)
    c: Coincident(g77,g78)
    c: Coincident(g78,g79)
    c: Coincident(g79,g80)
    c: Coincident(g80,g75)
    c: Equal(g75, g76-g80) x5
    c: PointOnObject(g75,g81)
    c: PointOnObject(g76,g81)
    c: PointOnObject(g77,g81)
    c: PointOnObject(g78,g81)
    c: PointOnObject(g79,g81)
    c: PointOnObject(g80,g81)
    c: PointOnObject(g81,g2)
    c: PointOnObject(g80,g2)
    c: Coincident(g82,g83)
    c: Coincident(g83,g84)
    c: Coincident(g84,g85)
    c: Coincident(g85,g86)
    c: Coincident(g86,g87)
    c: Coincident(g87,g82)
    c: Equal(g82, g83-g87) x5
    c: PointOnObject(g82,g88)
    c: PointOnObject(g83,g88)
    c: PointOnObject(g84,g88)
    c: PointOnObject(g85,g88)
    c: PointOnObject(g86,g88)
    c: PointOnObject(g87,g88)
    c: PointOnObject(g88,g2)
    c: PointOnObject(g87,g2)
    c: Coincident(g89,g90)
    c: Coincident(g90,g91)
    c: Coincident(g91,g92)
    c: Coincident(g92,g93)
    c: Coincident(g93,g94)
    c: Coincident(g94,g89)
    c: Equal(g89, g90-g94) x5
    c: PointOnObject(g89,g95)
    c: PointOnObject(g90,g95)
    c: PointOnObject(g91,g95)
    c: PointOnObject(g92,g95)
    c: PointOnObject(g93,g95)
    c: PointOnObject(g94,g95)
    c: PointOnObject(g95,g2)
    c: PointOnObject(g94,g2)
    c: Coincident(g96,g97)
    c: Coincident(g97,g98)
    c: Coincident(g98,g99)
    c: Coincident(g99,g100)
    c: Coincident(g100,g101)
    c: Coincident(g101,g96)
    c: Equal(g96, g97-g101) x5
    c: PointOnObject(g96,g102)
    c: PointOnObject(g97,g102)
    c: PointOnObject(g98,g102)
    c: PointOnObject(g99,g102)
    c: PointOnObject(g100,g102)
    c: PointOnObject(g101,g102)
    c: PointOnObject(g102,g3)
    c: PointOnObject(g101,g3)
    c: Coincident(g103,g104)
    c: Coincident(g104,g105)
    c: Coincident(g105,g106)
    c: Coincident(g106,g107)
    c: Coincident(g107,g108)
    c: Coincident(g108,g103)
    c: Equal(g103, g104-g108) x5
    c: PointOnObject(g103,g109)
    c: PointOnObject(g104,g109)
    c: PointOnObject(g105,g109)
    c: PointOnObject(g106,g109)
    c: PointOnObject(g107,g109)
    c: PointOnObject(g108,g109)
    c: PointOnObject(g109,g3)
    c: PointOnObject(g108,g3)
    c: Coincident(g110,g111)
    c: Coincident(g111,g112)
    c: Coincident(g112,g113)
    c: Coincident(g113,g114)
    c: Coincident(g114,g115)
    c: Coincident(g115,g110)
    c: Equal(g110, g111-g115) x5
    c: PointOnObject(g110,g116)
    c: PointOnObject(g111,g116)
    c: PointOnObject(g112,g116)
    c: PointOnObject(g113,g116)
    c: PointOnObject(g114,g116)
    c: PointOnObject(g115,g116)
    c: PointOnObject(g116,g25)
    c: PointOnObject(g115,g25)
    c: Coincident(g117,g118)
    c: Coincident(g118,g119)
    c: Coincident(g119,g120)
    c: Coincident(g120,g121)
    c: Coincident(g121,g122)
    c: Coincident(g122,g117)
    c: Equal(g117, g118-g122) x5
    c: PointOnObject(g117,g123)
    c: PointOnObject(g118,g123)
    c: PointOnObject(g119,g123)
    c: PointOnObject(g120,g123)
    c: PointOnObject(g121,g123)
    c: PointOnObject(g122,g123)
    c: PointOnObject(g123,g25)
    c: PointOnObject(g122,g25)
    c: Coincident(g124,g125)
    c: Coincident(g125,g126)
    c: Coincident(g126,g127)
    c: Coincident(g127,g128)
    c: Coincident(g128,g129)
    c: Coincident(g129,g124)
    c: Equal(g124, g125-g129) x5
    c: PointOnObject(g124,g130)
    c: PointOnObject(g125,g130)
    c: PointOnObject(g126,g130)
    c: PointOnObject(g127,g130)
    c: PointOnObject(g128,g130)
    c: PointOnObject(g129,g130)
    c: PointOnObject(g130,g25)
    c: PointOnObject(g129,g25)
    c: Coincident(g131,g132)
    c: Coincident(g132,g133)
    c: Coincident(g133,g134)
    c: Coincident(g134,g135)
    c: Coincident(g135,g136)
    c: Coincident(g136,g131)
    c: Equal(g131, g132-g136) x5
    c: PointOnObject(g131,g137)
    c: PointOnObject(g132,g137)
    c: PointOnObject(g133,g137)
    c: PointOnObject(g134,g137)
    c: PointOnObject(g135,g137)
    c: PointOnObject(g136,g137)
    c: PointOnObject(g137,g25)
    c: PointOnObject(g136,g25)
    c: PointOnObject(g67,g46)
    c: PointOnObject(g81,g44)
    c: PointOnObject(g88,g42)
    c: PointOnObject(g95,g40)
    c: PointOnObject(g102,g41)
    c: PointOnObject(g109,g43)
    c: PointOnObject(g74,g45)
    c: PointOnObject(g137,g46)
    c: PointOnObject(g130,g44)
    c: PointOnObject(g123,g42)
    c: PointOnObject(g116,g40)
    c: Radius(g95) = 18
    c: Radius(g88) = 18
    c: Radius(g81) = 18
    c: Radius(g53) = 18
    c: Radius(g60) = 18
    c: Radius(g67) = 18
    c: Radius(g74) = 18
    c: Radius(g109) = 18
    c: Radius(g102) = 18
    c: Radius(g116) = 18
    c: Radius(g123) = 18
    c: Radius(g130) = 18
    c: Radius(g137) = 18
    c: PointOnObject(g53,g45)
    c: PointOnObject(g60,g46)
FEATURE [PartDesign::Pocket] Pocket004
  BaseFeature = -> Pocket003
  Direction = (0,0,-1)
  Length = 5
  Length2 = 5
  Profile = -> Sketch010
  ReferenceAxis = -> Sketch010 [N_Axis]
  Type = 1
FEATURE [PartDesign::Body] Body001  label="Back"
  Group = -> [Sketch005,Pad004,Pad005,Pad006,Sketch006,Pocket002,Pad007,Sketch007,Sketch008,Pad008,Sketch009,Pocket003,Sketch010,Pocket004]
  Origin = -> Origin001
  Tip = -> Pocket004
note: 2 file-system paths scrubbed to <path> (originals preserved in the JSON sidecar)
